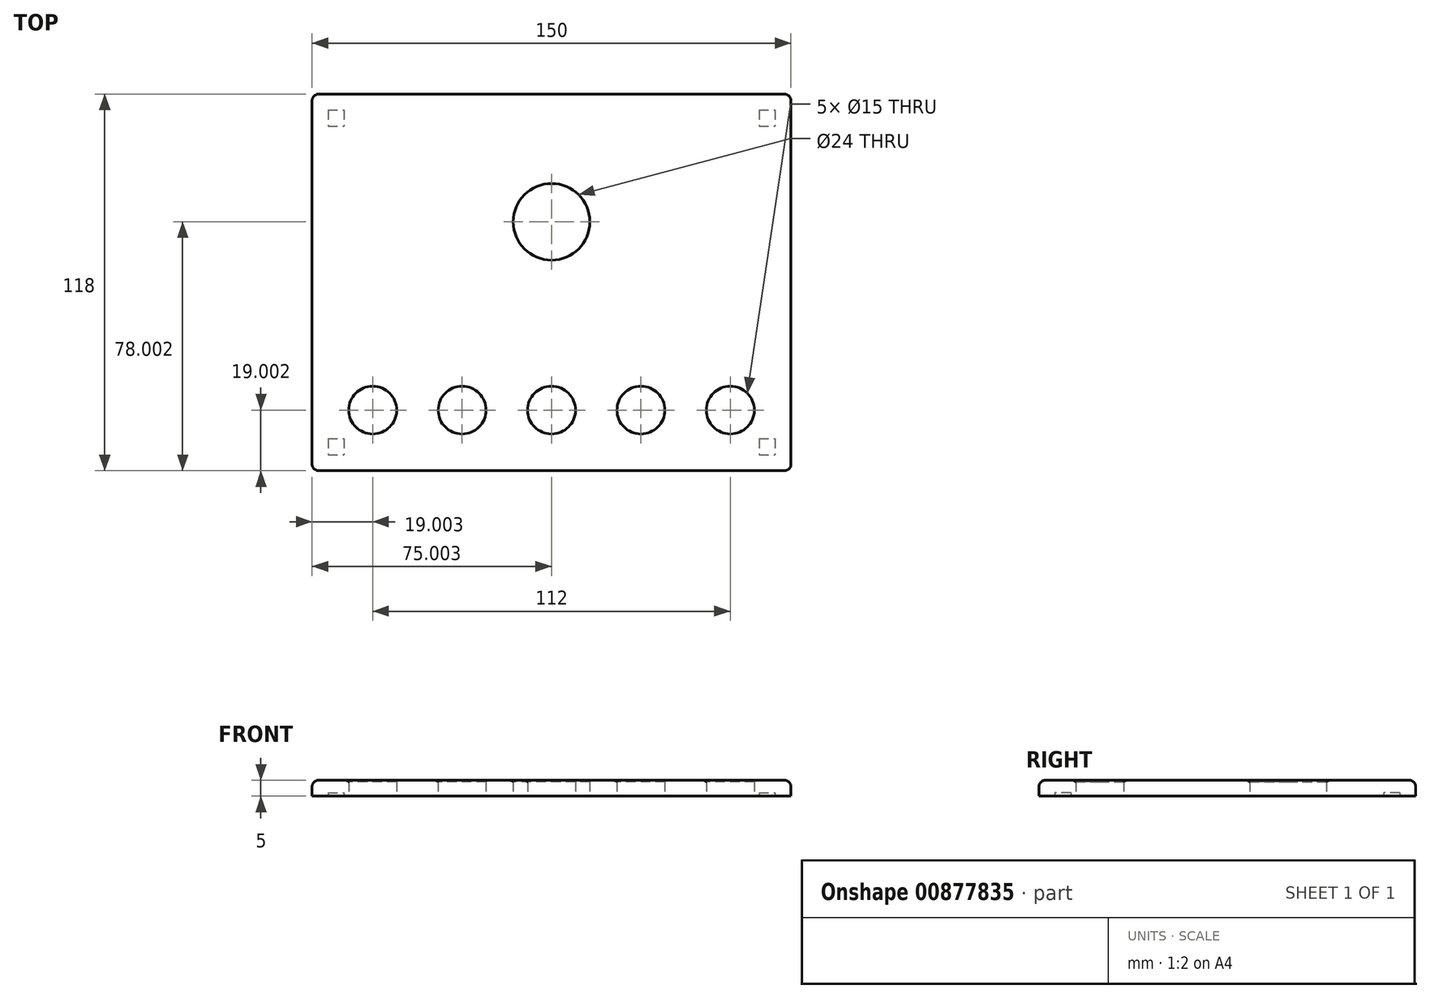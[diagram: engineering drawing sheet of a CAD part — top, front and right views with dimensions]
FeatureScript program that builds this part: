
annotation { "Feature Type Name" : "Feature", "Feature Type Description" : "" }
export const myFeature = defineFeature(function(context is Context, id is Id, definition is map)
    precondition{}
    {
        {
            var Q0;
            Q0=qCreatedBy(makeId("Top.planeOp"),FACE);
            var sketch = newSketch(context, id + "F0", { "sketchPlane" : qUnion([Q0])});
            skLineSegment(sketch, "E0.bottom", {"start": v(-74.72, 52.9) * mm, "end": v(75.28, 52.9) * mm});
            skLineSegment(sketch, "E0.top", {"start": v(-74.72, -65.1) * mm, "end": v(75.28, -65.1) * mm});
            skLineSegment(sketch, "E0.left", {"start": v(-74.72, 52.9) * mm, "end": v(-74.72, -65.1) * mm});
            skLineSegment(sketch, "E0.right", {"start": v(75.28, 52.9) * mm, "end": v(75.28, -65.1) * mm});
            skCircle(sketch, "E1", {"center": v(-55.72, -46.1) * mm, "radius": 7.5 * mm});
            skCircle(sketch, "E2", {"center": v(-27.72, -46.1) * mm, "radius": 7.5 * mm});
            skCircle(sketch, "E3", {"center": v(0.28, -46.1) * mm, "radius": 7.5 * mm});
            skCircle(sketch, "E4", {"center": v(28.28, -46.1) * mm, "radius": 7.5 * mm});
            skCircle(sketch, "E5", {"center": v(56.28, -46.1) * mm, "radius": 7.5 * mm});
            skCircle(sketch, "E6", {"center": v(0.28, 12.9) * mm, "radius": 12 * mm});
            skLineSegment(sketch, "E7.bottom", {"start": v(-69.72, -55.1) * mm, "end": v(-64.72, -55.1) * mm});
            skLineSegment(sketch, "E7.top", {"start": v(-69.72, -60.1) * mm, "end": v(-64.72, -60.1) * mm});
            skLineSegment(sketch, "E7.left", {"start": v(-69.72, -55.1) * mm, "end": v(-69.72, -60.1) * mm});
            skLineSegment(sketch, "E7.right", {"start": v(-64.72, -55.1) * mm, "end": v(-64.72, -60.1) * mm});
            skLineSegment(sketch, "E8.bottom", {"start": v(-69.72, 47.9) * mm, "end": v(-64.72, 47.9) * mm});
            skLineSegment(sketch, "E8.top", {"start": v(-69.72, 42.9) * mm, "end": v(-64.72, 42.9) * mm});
            skLineSegment(sketch, "E8.left", {"start": v(-69.72, 47.9) * mm, "end": v(-69.72, 42.9) * mm});
            skLineSegment(sketch, "E8.right", {"start": v(-64.72, 47.9) * mm, "end": v(-64.72, 42.9) * mm});
            skLineSegment(sketch, "E9.bottom", {"start": v(65.28, -55.1) * mm, "end": v(70.28, -55.1) * mm});
            skLineSegment(sketch, "E9.top", {"start": v(65.28, -60.1) * mm, "end": v(70.28, -60.1) * mm});
            skLineSegment(sketch, "E9.left", {"start": v(65.28, -55.1) * mm, "end": v(65.28, -60.1) * mm});
            skLineSegment(sketch, "E9.right", {"start": v(70.28, -55.1) * mm, "end": v(70.28, -60.1) * mm});
            skLineSegment(sketch, "E10.bottom", {"start": v(65.28, 47.9) * mm, "end": v(70.28, 47.9) * mm});
            skLineSegment(sketch, "E10.top", {"start": v(65.28, 42.9) * mm, "end": v(70.28, 42.9) * mm});
            skLineSegment(sketch, "E10.left", {"start": v(65.28, 47.9) * mm, "end": v(65.28, 42.9) * mm});
            skLineSegment(sketch, "E10.right", {"start": v(70.28, 47.9) * mm, "end": v(70.28, 42.9) * mm});
            skSolve(sketch);
        }
        {
            var Q0;
            Q0 = qSketchRegion(id + "F0", true);
            var Q1;
            Q1=makeQuery(id+"F0.imprint","IMPRINT",FACE,{"disambiguationData":[TD([[makeQuery(id+"F0.imprint","IMPRINT",EDGE,{"derivedFrom":sQuery(id+"F0.wireOp",EDGE,"E7.bottom")}),-1.0]])]});
            var Q2;
            Q2=makeQuery(id+"F0.imprint","IMPRINT",FACE,{"disambiguationData":[TD([[makeQuery(id+"F0.imprint","IMPRINT",EDGE,{"derivedFrom":sQuery(id+"F0.wireOp",EDGE,"E8.bottom")}),-1.0]])]});
            var Q3;
            Q3=makeQuery(id+"F0.imprint","IMPRINT",FACE,{"disambiguationData":[TD([[makeQuery(id+"F0.imprint","IMPRINT",EDGE,{"derivedFrom":sQuery(id+"F0.wireOp",EDGE,"E10.bottom")}),-1.0]])]});
            var Q4;
            Q4=makeQuery(id+"F0.imprint","IMPRINT",FACE,{"disambiguationData":[TD([[makeQuery(id+"F0.imprint","IMPRINT",EDGE,{"derivedFrom":sQuery(id+"F0.wireOp",EDGE,"E9.bottom")}),-1.0]])]});
            extrude(context, id + "F1", {"entities" : qUnion([Q0, Q1, Q2, Q3, Q4]), "depth" : 5 * mm, "offsetDistance" : 25 * mm});
        }
        {
            var Q0;
            Q0=makeQuery(id+"F0.imprint","IMPRINT",FACE,{"disambiguationData":[TD([[makeQuery(id+"F0.imprint","IMPRINT",EDGE,{"derivedFrom":sQuery(id+"F0.wireOp",EDGE,"E8.bottom")}),-1.0]])]});
            var Q1;
            Q1=makeQuery(id+"F0.imprint","IMPRINT",FACE,{"disambiguationData":[TD([[makeQuery(id+"F0.imprint","IMPRINT",EDGE,{"derivedFrom":sQuery(id+"F0.wireOp",EDGE,"E10.bottom")}),-1.0]])]});
            var Q2;
            Q2=makeQuery(id+"F0.imprint","IMPRINT",FACE,{"disambiguationData":[TD([[makeQuery(id+"F0.imprint","IMPRINT",EDGE,{"derivedFrom":sQuery(id+"F0.wireOp",EDGE,"E9.bottom")}),-1.0]])]});
            var Q3;
            Q3=makeQuery(id+"F0.imprint","IMPRINT",FACE,{"disambiguationData":[TD([[makeQuery(id+"F0.imprint","IMPRINT",EDGE,{"derivedFrom":sQuery(id+"F0.wireOp",EDGE,"E7.bottom")}),-1.0]])]});
            extrude(context, id + "F2", {"entities" : qUnion([Q0, Q1, Q2, Q3]), "operationType" : NewBodyOperationType.REMOVE, "depth" : 1 * mm, "offsetDistance" : 25 * mm});
        }
        {
            var Q0;
            Q0=makeQuery(id+"F1.opExtrude","CAP_EDGE",EDGE,{"disambiguationData":[OSD([sQuery(id+"F0.wireOp",EDGE,"E6")])],"isStart":false});
            var Q1;
            Q1=makeQuery(id+"F1.opExtrude","CAP_EDGE",EDGE,{"disambiguationData":[OSD([sQuery(id+"F0.wireOp",EDGE,"E1")])],"isStart":false});
            var Q2;
            Q2=makeQuery(id+"F1.opExtrude","CAP_EDGE",EDGE,{"disambiguationData":[OSD([sQuery(id+"F0.wireOp",EDGE,"E2")])],"isStart":false});
            var Q3;
            Q3=makeQuery(id+"F1.opExtrude","CAP_EDGE",EDGE,{"disambiguationData":[OSD([sQuery(id+"F0.wireOp",EDGE,"E3")])],"isStart":false});
            var Q4;
            Q4=makeQuery(id+"F1.opExtrude","CAP_EDGE",EDGE,{"disambiguationData":[OSD([sQuery(id+"F0.wireOp",EDGE,"E4")])],"isStart":false});
            var Q5;
            Q5=makeQuery(id+"F1.opExtrude","CAP_EDGE",EDGE,{"disambiguationData":[OSD([sQuery(id+"F0.wireOp",EDGE,"E5")])],"isStart":false});
            chamfer(context, id + "F3", {"entities" : qUnion([Q0, Q1, Q2, Q3, Q4, Q5]), "width" : 0.5 * mm});
        }
        {
            var Q0;
            Q0=makeQuery(id+"F1.opExtrude","CAP_FACE",FACE,{"disambiguationData":[OSD([sQuery(id+"F0.wireOp",EDGE,"E0.bottom"),sQuery(id+"F0.wireOp",EDGE,"E0.top"),sQuery(id+"F0.wireOp",EDGE,"E0.left"),sQuery(id+"F0.wireOp",EDGE,"E0.right"),sQuery(id+"F0.wireOp",EDGE,"E1"),sQuery(id+"F0.wireOp",EDGE,"E2"),sQuery(id+"F0.wireOp",EDGE,"E3"),sQuery(id+"F0.wireOp",EDGE,"E4"),sQuery(id+"F0.wireOp",EDGE,"E5"),sQuery(id+"F0.wireOp",EDGE,"E6")])],"isStart":false});
            fillet(context, id + "F4", {"entities" : qUnion([Q0]), "radius" : 2 * mm, "allowEdgeOverflow" : false});
        }
        {
            var Q0;
            Q0=makeQuery(id+"F4.opFillet","BLEND_FACE",FACE,{"disambiguationData":[OSD([sQuery(id+"F0.wireOp",EDGE,"E0.right")])]});
            var Q1;
            Q1=makeQuery(id+"F4.opFillet","BLEND_FACE",FACE,{"disambiguationData":[OSD([sQuery(id+"F0.wireOp",EDGE,"E0.top")])]});
            var Q2;
            {var subQ0=sQuery(id+"F0.wireOp",EDGE,"E0.left");Q2=makeQuery(id+"F4.opFillet","BLEND_EDGE",EDGE,{"blendedFrom":[makeQuery(id+"F1.opExtrude","CAP_EDGE",EDGE,{"disambiguationData":[OSD([subQ0])],"isStart":false}),makeQuery(id+"F1.opExtrude","CAP_FACE",FACE,{"disambiguationData":[OSD([sQuery(id+"F0.wireOp",EDGE,"E0.bottom"),sQuery(id+"F0.wireOp",EDGE,"E0.top"),subQ0,sQuery(id+"F0.wireOp",EDGE,"E0.right"),sQuery(id+"F0.wireOp",EDGE,"E1"),sQuery(id+"F0.wireOp",EDGE,"E2"),sQuery(id+"F0.wireOp",EDGE,"E3"),sQuery(id+"F0.wireOp",EDGE,"E4"),sQuery(id+"F0.wireOp",EDGE,"E5"),sQuery(id+"F0.wireOp",EDGE,"E6")])],"isStart":false})],"blendedInto":[makeQuery(id+"F1.opExtrude","CAP_FACE",FACE,{"disambiguationData":[OSD([sQuery(id+"F0.wireOp",EDGE,"E0.bottom"),sQuery(id+"F0.wireOp",EDGE,"E0.top"),subQ0,sQuery(id+"F0.wireOp",EDGE,"E0.right"),sQuery(id+"F0.wireOp",EDGE,"E1"),sQuery(id+"F0.wireOp",EDGE,"E2"),sQuery(id+"F0.wireOp",EDGE,"E3"),sQuery(id+"F0.wireOp",EDGE,"E4"),sQuery(id+"F0.wireOp",EDGE,"E5"),sQuery(id+"F0.wireOp",EDGE,"E6")])],"isStart":false})]});}
            var Q3;
            {var subQ0=sQuery(id+"F0.wireOp",EDGE,"E0.bottom");Q3=makeQuery(id+"F4.opFillet","BLEND_EDGE",EDGE,{"blendedFrom":[makeQuery(id+"F1.opExtrude","CAP_EDGE",EDGE,{"disambiguationData":[OSD([subQ0])],"isStart":false}),makeQuery(id+"F1.opExtrude","CAP_FACE",FACE,{"disambiguationData":[OSD([subQ0,sQuery(id+"F0.wireOp",EDGE,"E0.top"),sQuery(id+"F0.wireOp",EDGE,"E0.left"),sQuery(id+"F0.wireOp",EDGE,"E0.right"),sQuery(id+"F0.wireOp",EDGE,"E1"),sQuery(id+"F0.wireOp",EDGE,"E2"),sQuery(id+"F0.wireOp",EDGE,"E3"),sQuery(id+"F0.wireOp",EDGE,"E4"),sQuery(id+"F0.wireOp",EDGE,"E5"),sQuery(id+"F0.wireOp",EDGE,"E6")])],"isStart":false})],"blendedInto":[makeQuery(id+"F1.opExtrude","CAP_FACE",FACE,{"disambiguationData":[OSD([subQ0,sQuery(id+"F0.wireOp",EDGE,"E0.top"),sQuery(id+"F0.wireOp",EDGE,"E0.left"),sQuery(id+"F0.wireOp",EDGE,"E0.right"),sQuery(id+"F0.wireOp",EDGE,"E1"),sQuery(id+"F0.wireOp",EDGE,"E2"),sQuery(id+"F0.wireOp",EDGE,"E3"),sQuery(id+"F0.wireOp",EDGE,"E4"),sQuery(id+"F0.wireOp",EDGE,"E5"),sQuery(id+"F0.wireOp",EDGE,"E6")])],"isStart":false})]});}
            var Q4;
            Q4=makeQuery(id+"F4.opFillet","BLEND_EDGE",EDGE,{"blendedFrom":[makeQuery(id+"F1.opExtrude","CAP_EDGE",EDGE,{"disambiguationData":[OSD([sQuery(id+"F0.wireOp",EDGE,"E0.bottom")])],"isStart":false}),makeQuery(id+"F1.opExtrude","CAP_EDGE",EDGE,{"disambiguationData":[OSD([sQuery(id+"F0.wireOp",EDGE,"E0.left")])],"isStart":false})],"blendedInto":[]});
            fillet(context, id + "F5", {"entities" : qUnion([Q0, Q1, Q2, Q3, Q4]), "radius" : 2 * mm, "tangentPropagation" : true, "allowEdgeOverflow" : false});
        }
    });
